# Revit family: AFX-Odell-Outdoor_Sconce
name_source: partatom
category: Lighting Fixtures
units: mm (PartAtom-declared; Revit-internal decimal feet)

## family parameters
Cut with Voids When Loaded = No
Host = Face
Light Source = No
Part Type = Normal
Room Calculation Point = No
Round Connector Dimension = Use Diameter
Shared = No

## types (1)
- ODEW0709LAJENBK
    Apparent Load = 0 VA
    Assembly Code = D5020200
    Cage Finish = AFX - Black Steel
    Colour Rendering Index = 80
    Default Elevation = 48"
    Depth = 8"
    Description = Outdoor LED Wall Ceiling Light Polycarbonate Housing And Diffuser - 6 3/4"W x 8"D x 9"H
    Diffuser Finish = AFX - White Acrylic
    Height = 9"
    Housing Finish = AFX - Black Steel
    Keynote = 12500
    Manufacturer = AFX Inc
    Model = ODEW0709LAJENBK
    Power Factor = 1
    Product Documentation Link = https://www.afxinc.com
    Revit File Built By = https://servex-us.com
    Type Comments = Odell
    URL = https://www.afxinc.com
    Voltage = 120 V
    Wattage Comments = 9
    Width = 6 3/4"

## geometry (parser evidence)
native form markers: Sweep x4
no freeform markers — native parametric forms only
